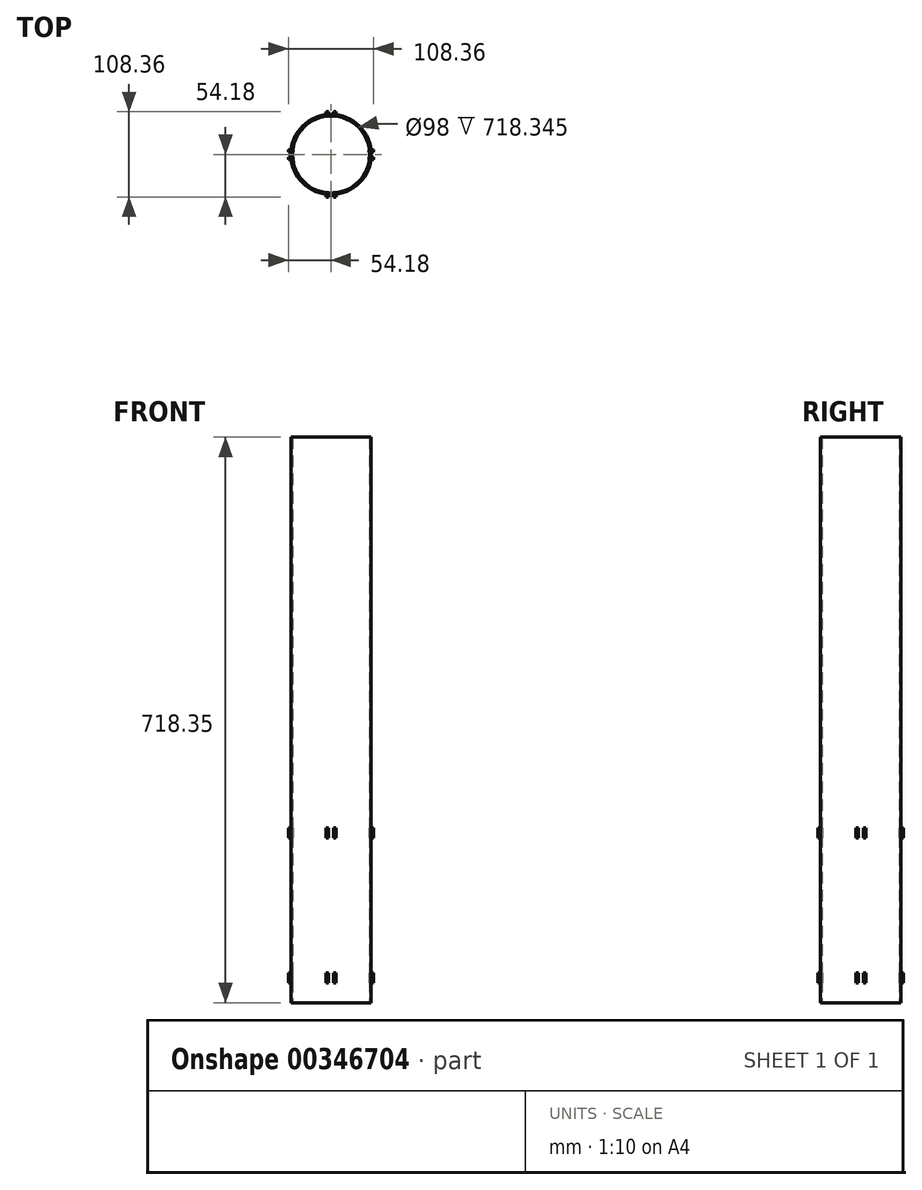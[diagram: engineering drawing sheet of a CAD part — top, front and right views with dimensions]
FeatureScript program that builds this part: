
annotation { "Feature Type Name" : "Feature", "Feature Type Description" : "" }
export const myFeature = defineFeature(function(context is Context, id is Id, definition is map)
    precondition{}
    {
        {
            var Q0;
            Q0=qCreatedBy(makeId("Top.planeOp"),FACE);
            var sketch = newSketch(context, id + "F0", { "sketchPlane" : qUnion([Q0])});
            skCircle(sketch, "E0", {"center": v(0, 0) * mm, "radius": 51 * mm});
            skCircle(sketch, "E1", {"center": v(0, 0) * mm, "radius": 49 * mm});
            skSolve(sketch);
        }
        {
            var Q0;
            Q0 = qSketchRegion(id + "F0", true);
            extrude(context, id + "F1", {"entities" : qUnion([Q0]), "depth" : 718.35 * mm});
        }
        {
            var Q0;
            Q0=qCreatedBy(makeId("Top.planeOp"),FACE);
            var sketch = newSketch(context, id + "F2", { "sketchPlane" : qUnion([Q0])});
            skLineSegment(sketch, "E2.bottom", {"start": v(51, -51) * mm, "end": v(-51, -51) * mm});
            skLineSegment(sketch, "E2.top", {"start": v(51, 51) * mm, "end": v(-51, 51) * mm});
            skLineSegment(sketch, "E2.left", {"start": v(51, -51) * mm, "end": v(51, 51) * mm});
            skLineSegment(sketch, "E2.right", {"start": v(-51, -51) * mm, "end": v(-51, 51) * mm});
            skPoint(sketch, "E2.middle", {"position": v(0, 0) * mm});
            skLineSegment(sketch, "E3", {"start": v(0, 0) * mm, "end": v(0, -51) * mm});
            skLineSegment(sketch, "E4", {"start": v(0, 0) * mm, "end": v(51, 0) * mm});
            skPoint(sketch, "E5.orphan", {"position": v(0, 2.55) * mm});
            skSolve(sketch);
        }
        {
            var Q0;
            Q0=sQuery(id+"F2.wireOp",EDGE,"E2.bottom");
            cPlane(context, id + "F3", {"entities" : qUnion([Q0]), "cplaneType" : CPlaneType.LINE_ANGLE, "offset" : 25.4 * mm, "angle" : 0 * degree, "width" : 152.4 * mm, "height" : 152.4 * mm});
        }
        {
            var Q0;
            Q0=qCreatedBy(id+"F3.planeOp",FACE);
            var sketch = newSketch(context, id + "F4", { "sketchPlane" : qUnion([Q0])});
            skLineSegment(sketch, "E6", {"start": v(0, 0) * mm, "end": v(0, 25.4) * mm});
            skLineSegment(sketch, "E7", {"start": v(0, 25.4) * mm, "end": v(0, 222.25) * mm});
            skLineSegment(sketch, "E8", {"start": v(0, 222.25) * mm, "end": v(3.18, 222.25) * mm});
            skLineSegment(sketch, "E9", {"start": v(3.18, 222.25) * mm, "end": v(-3.18, 222.25) * mm});
            skLineSegment(sketch, "E10", {"start": v(-3.18, 222.25) * mm, "end": v(-3.18, 209.55) * mm});
            skLineSegment(sketch, "E11", {"start": v(-3.18, 209.55) * mm, "end": v(-6.35, 209.56) * mm});
            skLineSegment(sketch, "E12", {"start": v(-6.35, 209.56) * mm, "end": v(-6.35, 222.26) * mm});
            skLineSegment(sketch, "E13", {"start": v(-6.35, 222.26) * mm, "end": v(-3.18, 222.25) * mm});
            skLineSegment(sketch, "E14.MirrorCS", {"start": v(6.35, 209.56) * mm, "end": v(6.35, 222.26) * mm});
            skLineSegment(sketch, "E15.MirrorCS", {"start": v(3.18, 222.25) * mm, "end": v(3.18, 209.55) * mm});
            skLineSegment(sketch, "E16.MirrorCS", {"start": v(6.35, 222.26) * mm, "end": v(3.18, 222.25) * mm});
            skLineSegment(sketch, "E17.MirrorCS", {"start": v(3.17, 209.55) * mm, "end": v(6.35, 209.56) * mm});
            skLineSegment(sketch, "E18", {"start": v(0, 123.83) * mm, "end": v(26.56, 123.83) * mm});
            skPoint(sketch, "E18.endSnap0", {"position": v(0, 123.83) * mm});
            skLineSegment(sketch, "E19.MirrorCS", {"start": v(3.17, 38.1) * mm, "end": v(6.35, 38.1) * mm});
            skLineSegment(sketch, "E20.MirrorCS", {"start": v(-3.17, 38.1) * mm, "end": v(-6.35, 38.1) * mm});
            skLineSegment(sketch, "E21.MirrorCS", {"start": v(6.35, 25.4) * mm, "end": v(3.18, 25.4) * mm});
            skLineSegment(sketch, "E22.MirrorCS", {"start": v(0, 25.4) * mm, "end": v(3.18, 25.4) * mm});
            skLineSegment(sketch, "E23.MirrorCS", {"start": v(3.18, 25.4) * mm, "end": v(-3.18, 25.4) * mm});
            skLineSegment(sketch, "E24.MirrorCS", {"start": v(-6.35, 25.4) * mm, "end": v(-3.18, 25.4) * mm});
            skLineSegment(sketch, "E25.MirrorCS", {"start": v(-3.18, 25.4) * mm, "end": v(-3.18, 38.1) * mm});
            skLineSegment(sketch, "E26.MirrorCS", {"start": v(6.35, 38.1) * mm, "end": v(6.35, 25.4) * mm});
            skLineSegment(sketch, "E27.MirrorCS", {"start": v(3.18, 25.4) * mm, "end": v(3.18, 38.1) * mm});
            skLineSegment(sketch, "E28.MirrorCS", {"start": v(-6.35, 38.1) * mm, "end": v(-6.35, 25.4) * mm});
            skSolve(sketch);
        }
        {
            var Q0;
            Q0 = qSketchRegion(id + "F4", true);
            extrude(context, id + "F5", {"entities" : qUnion([Q0]), "operationType" : NewBodyOperationType.ADD, "depth" : 3.17 * mm});
        }
        {
            var Q0;
            Q0=sQuery(id+"F2.wireOp",EDGE,"E2.left");
            cPlane(context, id + "F6", {"entities" : qUnion([Q0]), "cplaneType" : CPlaneType.LINE_ANGLE, "offset" : 25.4 * mm, "angle" : 90 * degree, "width" : 152.4 * mm, "height" : 152.4 * mm});
        }
        {
            var Q0;
            Q0=qCreatedBy(id+"F6.planeOp",FACE);
            var sketch = newSketch(context, id + "F7", { "sketchPlane" : qUnion([Q0])});
            skLineSegment(sketch, "E29", {"start": v(0, 0) * mm, "end": v(0, 25.4) * mm});
            skLineSegment(sketch, "E30", {"start": v(0, 25.4) * mm, "end": v(0, 222.25) * mm});
            skLineSegment(sketch, "E31", {"start": v(0, 222.25) * mm, "end": v(3.18, 222.25) * mm});
            skLineSegment(sketch, "E32", {"start": v(3.17, 222.25) * mm, "end": v(-3.18, 222.25) * mm});
            skLineSegment(sketch, "E33", {"start": v(-3.18, 222.25) * mm, "end": v(-3.18, 209.55) * mm});
            skLineSegment(sketch, "E34", {"start": v(-3.18, 209.55) * mm, "end": v(-6.35, 209.55) * mm});
            skLineSegment(sketch, "E35", {"start": v(-6.35, 209.55) * mm, "end": v(-6.35, 222.25) * mm});
            skLineSegment(sketch, "E36", {"start": v(-6.35, 222.25) * mm, "end": v(-3.18, 222.25) * mm});
            skLineSegment(sketch, "E37.MirrorCS", {"start": v(6.35, 222.25) * mm, "end": v(3.18, 222.25) * mm});
            skLineSegment(sketch, "E38.MirrorCS", {"start": v(6.35, 209.55) * mm, "end": v(6.35, 222.25) * mm});
            skLineSegment(sketch, "E39.MirrorCS", {"start": v(3.18, 209.55) * mm, "end": v(6.35, 209.55) * mm});
            skLineSegment(sketch, "E40.MirrorCS", {"start": v(3.18, 222.25) * mm, "end": v(3.18, 209.55) * mm});
            skLineSegment(sketch, "E41", {"start": v(0, 123.83) * mm, "end": v(31.92, 123.83) * mm});
            skLineSegment(sketch, "E42.MirrorCS", {"start": v(-3.18, 38.1) * mm, "end": v(-6.35, 38.1) * mm});
            skLineSegment(sketch, "E43.MirrorCS", {"start": v(3.18, 38.1) * mm, "end": v(6.35, 38.1) * mm});
            skLineSegment(sketch, "E44.MirrorCS", {"start": v(0, 25.4) * mm, "end": v(3.18, 25.4) * mm});
            skLineSegment(sketch, "E45.MirrorCS", {"start": v(3.17, 25.4) * mm, "end": v(-3.18, 25.4) * mm});
            skLineSegment(sketch, "E46.MirrorCS", {"start": v(-6.35, 25.4) * mm, "end": v(-3.18, 25.4) * mm});
            skLineSegment(sketch, "E47.MirrorCS", {"start": v(6.35, 25.4) * mm, "end": v(3.18, 25.4) * mm});
            skLineSegment(sketch, "E48.MirrorCS", {"start": v(-3.18, 25.4) * mm, "end": v(-3.18, 38.1) * mm});
            skLineSegment(sketch, "E49.MirrorCS", {"start": v(-6.35, 38.1) * mm, "end": v(-6.35, 25.4) * mm});
            skLineSegment(sketch, "E50.MirrorCS", {"start": v(3.18, 25.4) * mm, "end": v(3.18, 38.1) * mm});
            skLineSegment(sketch, "E51.MirrorCS", {"start": v(6.35, 38.1) * mm, "end": v(6.35, 25.4) * mm});
            skSolve(sketch);
        }
        {
            var Q0;
            Q0 = qSketchRegion(id + "F7", true);
            extrude(context, id + "F8", {"entities" : qUnion([Q0]), "depth" : 3.17 * mm});
        }
        {
            var Q0;
            Q0=sQuery(id+"F2.wireOp",EDGE,"E2.top");
            cPlane(context, id + "F9", {"entities" : qUnion([Q0]), "cplaneType" : CPlaneType.LINE_ANGLE, "offset" : 25.4 * mm, "angle" : 0 * degree, "width" : 152.4 * mm, "height" : 152.4 * mm});
        }
        {
            var Q0;
            Q0=qCreatedBy(id+"F9.planeOp",FACE);
            var sketch = newSketch(context, id + "F10", { "sketchPlane" : qUnion([Q0])});
            skLineSegment(sketch, "E52", {"start": v(0, 0) * mm, "end": v(0, 25.4) * mm});
            skLineSegment(sketch, "E53", {"start": v(0, 25.4) * mm, "end": v(0, 222.25) * mm});
            skLineSegment(sketch, "E54", {"start": v(0, 222.25) * mm, "end": v(-3.17, 222.25) * mm});
            skLineSegment(sketch, "E55", {"start": v(-3.17, 222.25) * mm, "end": v(3.17, 222.25) * mm});
            skLineSegment(sketch, "E56", {"start": v(3.17, 222.25) * mm, "end": v(3.17, 209.55) * mm});
            skLineSegment(sketch, "E57", {"start": v(3.17, 209.55) * mm, "end": v(6.35, 209.55) * mm});
            skLineSegment(sketch, "E58", {"start": v(6.35, 209.55) * mm, "end": v(6.35, 222.25) * mm});
            skLineSegment(sketch, "E59", {"start": v(6.35, 222.25) * mm, "end": v(3.17, 222.25) * mm});
            skLineSegment(sketch, "E60.MirrorCS", {"start": v(0, 222.25) * mm, "end": v(3.17, 222.25) * mm});
            skLineSegment(sketch, "E61.MirrorCS", {"start": v(-6.35, 209.55) * mm, "end": v(-6.35, 222.25) * mm});
            skLineSegment(sketch, "E62.MirrorCS", {"start": v(-3.17, 209.55) * mm, "end": v(-6.35, 209.55) * mm});
            skLineSegment(sketch, "E63.MirrorCS", {"start": v(-6.35, 222.25) * mm, "end": v(-3.17, 222.25) * mm});
            skLineSegment(sketch, "E64.MirrorCS", {"start": v(3.17, 222.25) * mm, "end": v(-3.17, 222.25) * mm});
            skLineSegment(sketch, "E65.MirrorCS", {"start": v(-3.17, 222.25) * mm, "end": v(-3.17, 209.55) * mm});
            skLineSegment(sketch, "E66", {"start": v(0, 123.83) * mm, "end": v(-38.57, 123.83) * mm});
            skPoint(sketch, "E66.endSnap0", {"position": v(0, 123.83) * mm});
            skLineSegment(sketch, "E67.MirrorCS", {"start": v(-3.17, 25.4) * mm, "end": v(3.17, 25.4) * mm});
            skLineSegment(sketch, "E68.MirrorCS", {"start": v(0, 25.4) * mm, "end": v(3.17, 25.4) * mm});
            skLineSegment(sketch, "E69.MirrorCS", {"start": v(0, 25.4) * mm, "end": v(-3.17, 25.4) * mm});
            skLineSegment(sketch, "E70.MirrorCS", {"start": v(3.17, 25.4) * mm, "end": v(-3.17, 25.4) * mm});
            skLineSegment(sketch, "E71.MirrorCS", {"start": v(6.35, 25.4) * mm, "end": v(3.17, 25.4) * mm});
            skLineSegment(sketch, "E72.MirrorCS", {"start": v(-6.35, 25.4) * mm, "end": v(-3.17, 25.4) * mm});
            skLineSegment(sketch, "E73.MirrorCS", {"start": v(3.17, 38.1) * mm, "end": v(6.35, 38.1) * mm});
            skLineSegment(sketch, "E74.MirrorCS", {"start": v(-3.17, 38.1) * mm, "end": v(-6.35, 38.1) * mm});
            skLineSegment(sketch, "E75.MirrorCS", {"start": v(3.17, 25.4) * mm, "end": v(3.17, 38.1) * mm});
            skLineSegment(sketch, "E76.MirrorCS", {"start": v(6.35, 38.1) * mm, "end": v(6.35, 25.4) * mm});
            skLineSegment(sketch, "E77.MirrorCS", {"start": v(-3.17, 25.4) * mm, "end": v(-3.17, 38.1) * mm});
            skLineSegment(sketch, "E78.MirrorCS", {"start": v(-6.35, 38.1) * mm, "end": v(-6.35, 25.4) * mm});
            skSolve(sketch);
        }
        {
            var Q0;
            Q0 = qSketchRegion(id + "F10", true);
            extrude(context, id + "F11", {"entities" : qUnion([Q0]), "operationType" : NewBodyOperationType.ADD, "oppositeDirection" : true, "depth" : 3.17 * mm});
        }
        {
            var Q0;
            Q0=sQuery(id+"F2.wireOp",EDGE,"E2.right");
            cPlane(context, id + "F12", {"entities" : qUnion([Q0]), "cplaneType" : CPlaneType.LINE_ANGLE, "offset" : 25.4 * mm, "angle" : 90 * degree, "width" : 152.4 * mm, "height" : 152.4 * mm});
        }
        {
            var Q0;
            Q0=qCreatedBy(id+"F12.planeOp",FACE);
            var sketch = newSketch(context, id + "F13", { "sketchPlane" : qUnion([Q0])});
            skLineSegment(sketch, "E79", {"start": v(0, 0) * mm, "end": v(0, 25.4) * mm});
            skLineSegment(sketch, "E80", {"start": v(0, 25.4) * mm, "end": v(0, 222.25) * mm});
            skLineSegment(sketch, "E81", {"start": v(0, 222.25) * mm, "end": v(-3.17, 222.25) * mm});
            skLineSegment(sketch, "E82", {"start": v(-3.17, 222.25) * mm, "end": v(3.17, 222.25) * mm});
            skLineSegment(sketch, "E83", {"start": v(3.17, 222.25) * mm, "end": v(3.17, 209.55) * mm});
            skLineSegment(sketch, "E84", {"start": v(3.17, 209.55) * mm, "end": v(6.35, 209.55) * mm});
            skLineSegment(sketch, "E85", {"start": v(6.35, 209.55) * mm, "end": v(6.35, 222.25) * mm});
            skLineSegment(sketch, "E86", {"start": v(6.35, 222.25) * mm, "end": v(3.17, 222.25) * mm});
            skLineSegment(sketch, "E87.MirrorCS", {"start": v(-6.35, 222.25) * mm, "end": v(-3.17, 222.25) * mm});
            skLineSegment(sketch, "E88.MirrorCS", {"start": v(-3.17, 209.55) * mm, "end": v(-6.35, 209.55) * mm});
            skLineSegment(sketch, "E89.MirrorCS", {"start": v(-3.17, 222.25) * mm, "end": v(-3.17, 209.55) * mm});
            skLineSegment(sketch, "E90.MirrorCS", {"start": v(-6.35, 209.55) * mm, "end": v(-6.35, 222.25) * mm});
            skLineSegment(sketch, "E91", {"start": v(0, 123.83) * mm, "end": v(-22.56, 123.83) * mm});
            skPoint(sketch, "E91.endSnap0", {"position": v(0, 123.83) * mm});
            skLineSegment(sketch, "E92.MirrorCS", {"start": v(3.17, 38.1) * mm, "end": v(6.35, 38.1) * mm});
            skLineSegment(sketch, "E93.MirrorCS", {"start": v(6.35, 25.4) * mm, "end": v(3.17, 25.4) * mm});
            skLineSegment(sketch, "E94.MirrorCS", {"start": v(-6.35, 25.4) * mm, "end": v(-3.17, 25.4) * mm});
            skLineSegment(sketch, "E95.MirrorCS", {"start": v(-3.17, 38.1) * mm, "end": v(-6.35, 38.1) * mm});
            skLineSegment(sketch, "E96.MirrorCS", {"start": v(-3.17, 25.4) * mm, "end": v(3.17, 25.4) * mm});
            skLineSegment(sketch, "E97.MirrorCS", {"start": v(0, 25.4) * mm, "end": v(-3.17, 25.4) * mm});
            skLineSegment(sketch, "E98.MirrorCS", {"start": v(3.17, 25.4) * mm, "end": v(3.17, 38.1) * mm});
            skLineSegment(sketch, "E99.MirrorCS", {"start": v(6.35, 38.1) * mm, "end": v(6.35, 25.4) * mm});
            skLineSegment(sketch, "E100.MirrorCS", {"start": v(-3.17, 25.4) * mm, "end": v(-3.17, 38.1) * mm});
            skLineSegment(sketch, "E101.MirrorCS", {"start": v(-6.35, 38.1) * mm, "end": v(-6.35, 25.4) * mm});
            skSolve(sketch);
        }
        {
            var Q0;
            Q0 = qSketchRegion(id + "F13", true);
            extrude(context, id + "F14", {"entities" : qUnion([Q0]), "oppositeDirection" : true, "depth" : 3.17 * mm});
        }
        {
            var Q0;
            Q0=makeQuery(id+"F5.opExtrude","CAP_FACE",FACE,{"disambiguationData":[OSD([sQuery(id+"F4.wireOp",EDGE,"E19.MirrorCS"),sQuery(id+"F4.wireOp",EDGE,"E21.MirrorCS"),sQuery(id+"F4.wireOp",EDGE,"E26.MirrorCS"),sQuery(id+"F4.wireOp",EDGE,"E27.MirrorCS")])],"isStart":true});
            var Q1;
            Q1=makeQuery(id+"F5.opExtrude","CAP_FACE",FACE,{"disambiguationData":[OSD([sQuery(id+"F4.wireOp",EDGE,"E20.MirrorCS"),sQuery(id+"F4.wireOp",EDGE,"E24.MirrorCS"),sQuery(id+"F4.wireOp",EDGE,"E25.MirrorCS"),sQuery(id+"F4.wireOp",EDGE,"E28.MirrorCS")])],"isStart":true});
            var Q2;
            Q2=makeQuery(id+"F5.opExtrude","CAP_FACE",FACE,{"disambiguationData":[OSD([sQuery(id+"F4.wireOp",EDGE,"E14.MirrorCS"),sQuery(id+"F4.wireOp",EDGE,"E15.MirrorCS"),sQuery(id+"F4.wireOp",EDGE,"E16.MirrorCS"),sQuery(id+"F4.wireOp",EDGE,"E17.MirrorCS")])],"isStart":true});
            var Q3;
            Q3=makeQuery(id+"F5.opExtrude","CAP_FACE",FACE,{"disambiguationData":[OSD([sQuery(id+"F4.wireOp",EDGE,"E10"),sQuery(id+"F4.wireOp",EDGE,"E11"),sQuery(id+"F4.wireOp",EDGE,"E12"),sQuery(id+"F4.wireOp",EDGE,"E13")])],"isStart":true});
            extrude(context, id + "F15", {"entities" : qUnion([Q0, Q1, Q2, Q3]), "depth" : 2.54 * mm});
        }
        {
            var Q0;
            Q0=makeQuery(id+"F8.opExtrude","CAP_FACE",FACE,{"disambiguationData":[OSD([sQuery(id+"F7.wireOp",EDGE,"E37.MirrorCS"),sQuery(id+"F7.wireOp",EDGE,"E38.MirrorCS"),sQuery(id+"F7.wireOp",EDGE,"E39.MirrorCS"),sQuery(id+"F7.wireOp",EDGE,"E40.MirrorCS")])],"isStart":true});
            var Q1;
            Q1=makeQuery(id+"F8.opExtrude","CAP_FACE",FACE,{"disambiguationData":[OSD([sQuery(id+"F7.wireOp",EDGE,"E33"),sQuery(id+"F7.wireOp",EDGE,"E34"),sQuery(id+"F7.wireOp",EDGE,"E35"),sQuery(id+"F7.wireOp",EDGE,"E36")])],"isStart":true});
            var Q2;
            Q2=makeQuery(id+"F8.opExtrude","CAP_FACE",FACE,{"disambiguationData":[OSD([sQuery(id+"F7.wireOp",EDGE,"E42.MirrorCS"),sQuery(id+"F7.wireOp",EDGE,"E46.MirrorCS"),sQuery(id+"F7.wireOp",EDGE,"E48.MirrorCS"),sQuery(id+"F7.wireOp",EDGE,"E49.MirrorCS")])],"isStart":true});
            var Q3;
            Q3=makeQuery(id+"F8.opExtrude","CAP_FACE",FACE,{"disambiguationData":[OSD([sQuery(id+"F7.wireOp",EDGE,"E43.MirrorCS"),sQuery(id+"F7.wireOp",EDGE,"E47.MirrorCS"),sQuery(id+"F7.wireOp",EDGE,"E50.MirrorCS"),sQuery(id+"F7.wireOp",EDGE,"E51.MirrorCS")])],"isStart":true});
            extrude(context, id + "F16", {"entities" : qUnion([Q0, Q1, Q2, Q3]), "depth" : 2.54 * mm});
        }
        {
            var Q0;
            Q0=makeQuery(id+"F11.opExtrude","CAP_FACE",FACE,{"disambiguationData":[OSD([sQuery(id+"F10.wireOp",EDGE,"E56"),sQuery(id+"F10.wireOp",EDGE,"E57"),sQuery(id+"F10.wireOp",EDGE,"E58"),sQuery(id+"F10.wireOp",EDGE,"E59")])],"isStart":true});
            var Q1;
            Q1=makeQuery(id+"F11.opExtrude","CAP_FACE",FACE,{"disambiguationData":[OSD([sQuery(id+"F10.wireOp",EDGE,"E61.MirrorCS"),sQuery(id+"F10.wireOp",EDGE,"E62.MirrorCS"),sQuery(id+"F10.wireOp",EDGE,"E63.MirrorCS"),sQuery(id+"F10.wireOp",EDGE,"E65.MirrorCS")])],"isStart":true});
            var Q2;
            Q2=makeQuery(id+"F11.opExtrude","CAP_FACE",FACE,{"disambiguationData":[OSD([sQuery(id+"F10.wireOp",EDGE,"E72.MirrorCS"),sQuery(id+"F10.wireOp",EDGE,"E74.MirrorCS"),sQuery(id+"F10.wireOp",EDGE,"E77.MirrorCS"),sQuery(id+"F10.wireOp",EDGE,"E78.MirrorCS")])],"isStart":true});
            var Q3;
            Q3=makeQuery(id+"F11.opExtrude","CAP_FACE",FACE,{"disambiguationData":[OSD([sQuery(id+"F10.wireOp",EDGE,"E71.MirrorCS"),sQuery(id+"F10.wireOp",EDGE,"E73.MirrorCS"),sQuery(id+"F10.wireOp",EDGE,"E75.MirrorCS"),sQuery(id+"F10.wireOp",EDGE,"E76.MirrorCS")])],"isStart":true});
            extrude(context, id + "F17", {"entities" : qUnion([Q0, Q1, Q2, Q3]), "depth" : 2.54 * mm});
        }
        {
            var Q0;
            Q0=makeQuery(id+"F14.opExtrude","CAP_FACE",FACE,{"disambiguationData":[OSD([sQuery(id+"F13.wireOp",EDGE,"E87.MirrorCS"),sQuery(id+"F13.wireOp",EDGE,"E88.MirrorCS"),sQuery(id+"F13.wireOp",EDGE,"E89.MirrorCS"),sQuery(id+"F13.wireOp",EDGE,"E90.MirrorCS")])],"isStart":true});
            var Q1;
            Q1=makeQuery(id+"F14.opExtrude","CAP_FACE",FACE,{"disambiguationData":[OSD([sQuery(id+"F13.wireOp",EDGE,"E83"),sQuery(id+"F13.wireOp",EDGE,"E84"),sQuery(id+"F13.wireOp",EDGE,"E85"),sQuery(id+"F13.wireOp",EDGE,"E86")])],"isStart":true});
            var Q2;
            Q2=makeQuery(id+"F14.opExtrude","CAP_FACE",FACE,{"disambiguationData":[OSD([sQuery(id+"F13.wireOp",EDGE,"E94.MirrorCS"),sQuery(id+"F13.wireOp",EDGE,"E95.MirrorCS"),sQuery(id+"F13.wireOp",EDGE,"E100.MirrorCS"),sQuery(id+"F13.wireOp",EDGE,"E101.MirrorCS")])],"isStart":true});
            var Q3;
            Q3=makeQuery(id+"F14.opExtrude","CAP_FACE",FACE,{"disambiguationData":[OSD([sQuery(id+"F13.wireOp",EDGE,"E92.MirrorCS"),sQuery(id+"F13.wireOp",EDGE,"E93.MirrorCS"),sQuery(id+"F13.wireOp",EDGE,"E98.MirrorCS"),sQuery(id+"F13.wireOp",EDGE,"E99.MirrorCS")])],"isStart":true});
            extrude(context, id + "F18", {"entities" : qUnion([Q0, Q1, Q2, Q3]), "depth" : 2.54 * mm});
        }
    });
